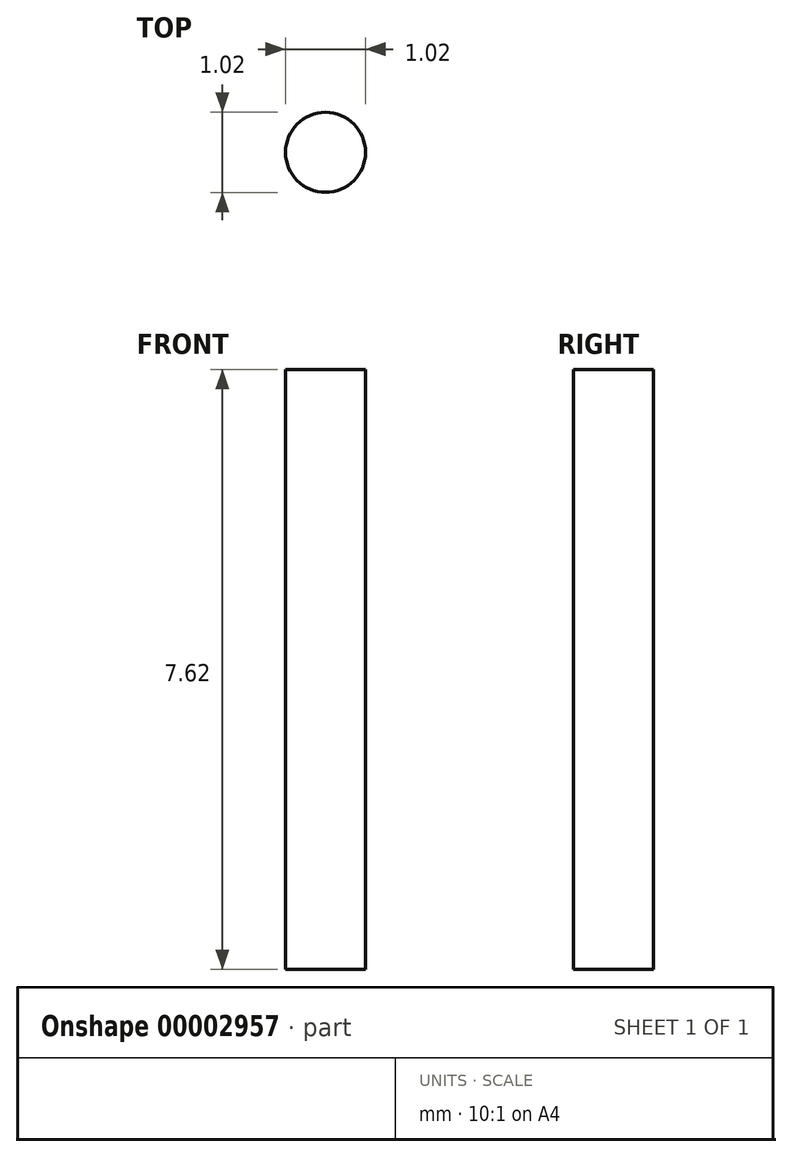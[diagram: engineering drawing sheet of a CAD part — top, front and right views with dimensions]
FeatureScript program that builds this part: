
annotation { "Feature Type Name" : "Feature", "Feature Type Description" : "" }
export const myFeature = defineFeature(function(context is Context, id is Id, definition is map)
    precondition{}
    {
        {
            var Q0;
            Q0=qCreatedBy(makeId("Top.planeOp"),FACE);
            var sketch = newSketch(context, id + "F0", { "sketchPlane" : qUnion([Q0])});
            skCircle(sketch, "E0", {"center": v(0, 0) * mm, "radius": 0.5 * mm});
            skSolve(sketch);
        }
        {
            var Q0;
            Q0=makeQuery(id+"F0.imprint","IMPRINT",FACE,{"disambiguationData":[TD([[makeQuery(id+"F0.imprint","IMPRINT",EDGE,{"derivedFrom":sQuery(id+"F0.wireOp",EDGE,"E0")}),1.0]])]});
            extrude(context, id + "F1", {"entities" : qUnion([Q0]), "depth" : 7.62 * mm});
        }
    });
